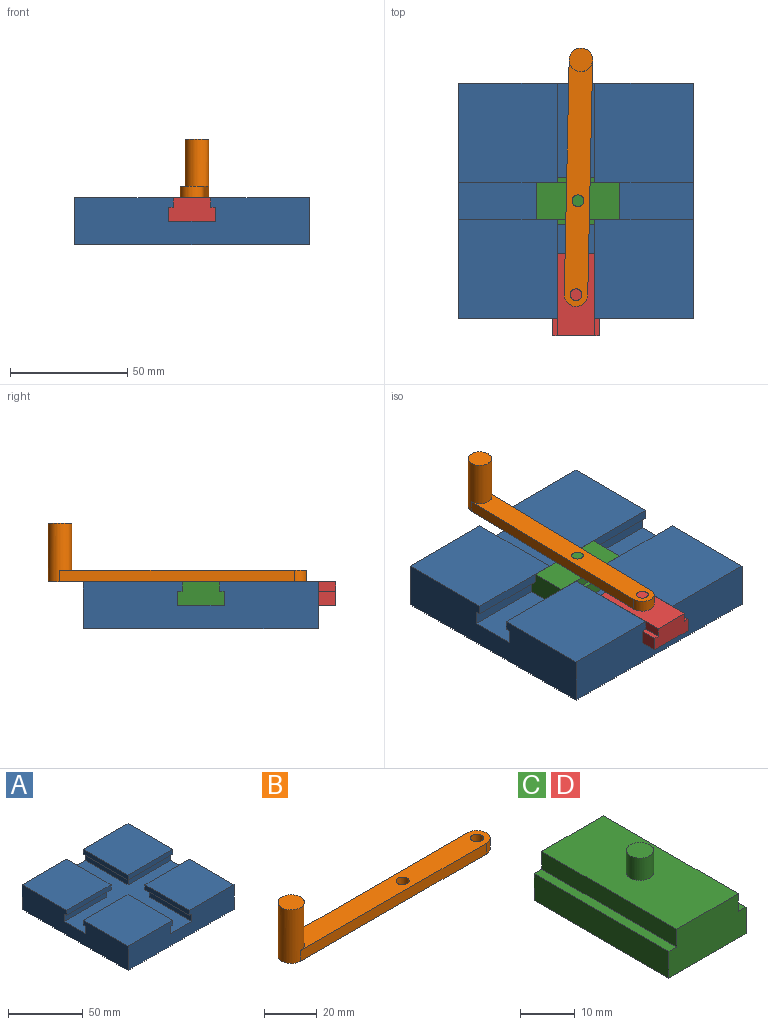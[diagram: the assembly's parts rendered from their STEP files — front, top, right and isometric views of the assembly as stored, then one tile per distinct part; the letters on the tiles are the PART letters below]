
ASSEMBLY  parts=4 mates=4
PART A: 30 faces, bbox 100x100x20 mm
  f0: plane 42x42mm, normal (0,0,1), area 1764mm2, adj f7,f9,f11,f24
  f1: plane 42x42mm, normal (0,0,1), area 1764mm2, adj f4,f9,f10,f29
  f2: plane 42x42mm, normal (0,0,-1), area 164mm2, adj f4,f5,f9,f10,f27,f29
  f3: plane 42x42mm, normal (0,0,-1), area 164mm2, adj f11,f12,f19,f21,f22,f25
  f4: plane 42x4mm, normal (1,0,0), area 168mm2, adj f1,f2,f9,f29
  f5: plane 40x6mm, normal (1,0,0), area 240mm2, adj f2,f9,f18,f27
  f6: plane 40x6mm, normal (-1,0,0), area 240mm2, adj f9,f18,f20,f23
  f7: plane 42x4mm, normal (-1,0,0), area 168mm2, adj f0,f9,f20,f24
  f8: plane 42x42mm, normal (0,0,1), area 1764mm2, adj f11,f12,f21,f22
  f9: plane 100x20mm, normal (0,-1,0), area 1816mm2, adj f0,f1,f2,f4,f5,f6,f7,f10
  f10: plane 100x20mm, normal (-1,0,0), area 1816mm2, adj f1,f2,f9,f12,f13,f14,f16,f18
  f11: plane 100x20mm, normal (1,0,0), area 1816mm2, adj f0,f3,f8,f9,f12,f14,f18,f20
  f12: plane 100x20mm, normal (0,1,0), area 1816mm2, adj f3,f8,f10,f11,f13,f14,f15,f16
  f13: plane 42x42mm, normal (0,0,1), area 1764mm2, adj f10,f12,f15,f28
  f14: plane 100x100mm, normal (0,0,-1), area 10000mm2, adj f9,f10,f11,f12
  f15: plane 42x4mm, normal (1,0,0), area 168mm2, adj f12,f13,f16,f28
  f16: plane 42x42mm, normal (0,0,-1), area 164mm2, adj f10,f12,f15,f17,f26,f28
  f17: plane 40x6mm, normal (1,0,0), area 240mm2, adj f12,f16,f18,f26
  f18: plane 100x100mm, normal (0,0,1), area 3600mm2, adj f5,f6,f9,f10,f11,f12,f17,f19
  f19: plane 40x6mm, normal (-1,0,0), area 240mm2, adj f3,f12,f18,f25
  f20: plane 42x42mm, normal (0,0,-1), area 164mm2, adj f6,f7,f9,f11,f23,f24
  f21: plane 42x4mm, normal (-1,0,0), area 168mm2, adj f3,f8,f12,f22
  f22: plane 42x4mm, normal (0,-1,0), area 168mm2, adj f3,f8,f11,f21
  f23: plane 40x6mm, normal (0,1,0), area 240mm2, adj f6,f11,f18,f20
  f24: plane 42x4mm, normal (0,1,0), area 168mm2, adj f0,f7,f11,f20
  f25: plane 40x6mm, normal (0,-1,0), area 240mm2, adj f3,f11,f18,f19
  f26: plane 40x6mm, normal (0,-1,0), area 240mm2, adj f10,f16,f17,f18
  f27: plane 40x6mm, normal (0,1,0), area 240mm2, adj f2,f5,f10,f18
  f28: plane 42x4mm, normal (0,-1,0), area 168mm2, adj f10,f13,f15,f16
  f29: plane 42x4mm, normal (0,1,0), area 168mm2, adj f1,f2,f4,f10
PART B: 9 faces, bbox 110x10x25 mm
  f0: cylinder r=5mm len=25mm, axis (0,0,-1), area 706.9mm2, adj f1,f4,f6,f7,f8
  f1: plane 100x5mm, normal (0,-1,0), area 500mm2, adj f0,f2,f6,f7
  f2: cylinder r=5mm len=10mm, axis (0,0,-1), area 78.5mm2, adj f1,f4,f6,f7
  f3: cylinder r=2.5mm len=5mm, axis (0,0,-1), area 78.5mm2, adj f6,f7
  f4: plane 100x5mm, normal (0,1,0), area 500mm2, adj f0,f2,f6,f7
  f5: cylinder r=2.5mm len=5mm, axis (0,0,-1), area 78.5mm2, adj f6,f7
  f6: plane 105x10mm, normal (0,0,1), area 960.7mm2, adj f0,f1,f2,f3,f4,f5
  f7: plane 110x10mm, normal (0,0,-1), area 1039.3mm2, adj f0,f1,f2,f3,f4,f5
  f8: plane 10x10mm, normal (0,0,1), area 78.5mm2, adj f0
PART C: 12 faces, bbox 20x35x15 mm
  f0: plane 35x16mm, normal (0,0,1), area 540.4mm2, adj f1,f7,f8,f9,f10
  f1: plane 35x4mm, normal (-1,0,0), area 140mm2, adj f0,f2,f8,f9
  f2: plane 35x2mm, normal (0,0,1), area 70mm2, adj f1,f3,f8,f9
  f3: plane 35x6mm, normal (-1,0,0), area 210mm2, adj f2,f4,f8,f9
  f4: plane 35x20mm, normal (0,0,-1), area 700mm2, adj f3,f5,f8,f9
  f5: plane 35x6mm, normal (1,0,0), area 210mm2, adj f4,f6,f8,f9
  f6: plane 35x2mm, normal (0,0,1), area 70mm2, adj f5,f7,f8,f9
  f7: plane 35x4mm, normal (1,0,0), area 140mm2, adj f0,f6,f8,f9
  f8: plane 20x10mm, normal (0,1,0), area 184mm2, adj f0,f1,f2,f3,f4,f5,f6,f7
  f9: plane 20x10mm, normal (0,-1,0), area 184mm2, adj f0,f1,f2,f3,f4,f5,f6,f7
  f10: cylinder r=2.5mm len=5mm, axis (0,0,-1), area 78.5mm2, adj f0,f11
  f11: plane 5x5mm, normal (0,0,1), area 19.6mm2, adj f10
PART D: same geometry as C
PLACE A at identity fixed
PLACE B rot(axis=(0,0,-1),91.2deg) t=(57.08,109.88,20)mm
PLACE C rot(axis=(0,0,-1),90deg) t=(33.33,100,0)mm
PLACE D t=(0,-7.49,0)mm
MATE revolute B.f2 <-> D.f10  axis (0,0,1) through (50,10.01,25)mm
MATE slider D.f9 <-> A.f9  axis (0,-1,0) through (50,-7.49,10)mm
MATE slider C.f9 <-> A.f10  axis (-1,0,0) through (33.33,50,10)mm
MATE revolute B.f3 <-> C.f10  axis (0,0,1) through (50.83,50,25)mm
